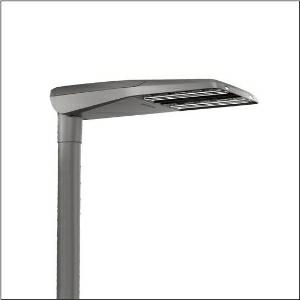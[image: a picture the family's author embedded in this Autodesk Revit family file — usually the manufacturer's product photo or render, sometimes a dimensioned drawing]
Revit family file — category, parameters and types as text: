
# Revit family: streetlight_sl_11_iq_midi___st1_0a_5xc3m41f08le_9450
name_source: partatom
category: Lighting Fixtures
units: mm (PartAtom-declared; Revit-internal decimal feet)

## family parameters
Cut with Voids When Loaded = No
Host = Face
Light Source = No
Part Type = Normal
Room Calculation Point = No
Round Connector Dimension = Use Diameter
Shared = No

## types (1)
- --- (1 x LED, 9290 lm, 60.4 W, 4000K)
    Apparent Load = 60 VA
    CIE Flux Codes = 33 66 96 100 100
    Color Rendering = 70
    Color Temperature = 4000K
    Default Elevation = 1800 mm
    Description = Streetlight SL 11 iQ midi, mast luminaire, primary light control with 3 zone facetted reflector, of plastic, silver coated, highly specular, primary optical cover: cover, of PMMA, transparent, light distribution: ST1.0a, light emission: direct distribution, primary light characteristic: asymmetric, installation type: post-top, side-entry, lamps: LED, High Power LED, rated values: 9.290lm | 60,4W | 153,8lm/W (begin service life); end service life: 9.290lm | 62,5W; at 50% lumin. flux: 4.645lm | 29,7W | 156,4lm/W, colour temperature: 4000K, colour rendering: CRI > 70, light colour: 740, light setting 1 begin service life: 100% | 9.290lm | 60,4W | 153,8lm/W | 4.000K, light setting 1 end service life: 62,5W, further light settings possible, control: optimised constant luminous flux control (CLO 2.0), Street-Remote, Desk-Remote (wireless, voltage-free reading and setting of iQ features in the workshop via application-optimized NFC function/RFID function), Light-Fading, Smart-Wire, Night-Set, Lumen-Switch, Temp-Guard, Auto-Match, with cable H07RN-F 5x 1.5mm², mains connection: 230..240V, AC, 50/60Hz, connection cable pre-assembled, cable length: 8,5m, luminaire housing, of diecast aluminium, powder-coated, Siteco® metallic grey (DB 702S), please order mast flange separately, inclination adjustable without tools: 0°, 5°, 10°, 15° (post-top) | 0°, -5°, -10°, -15° (side-entry), sealing non-destructively replaceable, multi-level sealing system, length: 780mm, width: 376mm, height: 118mm, mast flange for spigot size: 42mm (side-entry): 5XC10008XM4, 60/48mm (side-entry/post-top): 5XC10108XM2, 76/60mm (side-entry/post-top): 5XC10108XM1, equipment: standard, protection rating (complete): IP66, insulation class (complete): insulation class II (safety insulation), certification: CE, ENEC, ENEC+, VDE, impact resistance: IK10, permissible operating ambient temperature for outdoor applications: -25..+50°C, standard-compliant lighting for roads and squares, Environmental Product Declaration (EPD) tested and certified by an independent institute, packaging unit: 1 piece

Light Distribution: ST1.0a
    Height = 118 mm
    Lamp = 1 x LED
    Lamp Light Flux = 9290 lm
    Lamp Power = 60.4 W
    Lamp count = 1
    Length = 780 mm
    Luminous efficacy = 154 lm/W
    Manufacturer = Siteco
    ModVariant = No
    Model = 5XC3M41F08LE
    Number of Poles = 1
    OnlyDefault = Yes
    Power Factor = 1
    Product Name = Streetlight SL 11 iQ midi | ST1.0a
    Product group = mast luminaire | pylon top
    ProductGroupID = 6100
    Protection Class = Protection class II
    Protection Degree = IP 66
    RLX_Detail_Level = 1
    RLX_Emergency_Light_Flux = 0 lm
    RLX_Emergency_Type = 0
    RLX_Emergency_Type_DB = No
    RlxData = <blob elided: 70313 chars, md5=c460e52b>
    Socket = socket
    Standby Power = 0 W
    System Light Flux = 9290 lm
    System Power = 60 W
    Type Comments = factory setting: luminous flux: 100 % | dim-lin: 254 | 520 mA
    Type Image = l_1005960.jpg
    URL = http://relux.com
    VarID = @adj_110121
    Voltage = 0 V
    Weight = 0.00 kg
    Width = 376 mm

## geometry (parser evidence)
native form markers: Blend x4, Sweep x11
no freeform markers — native parametric forms only
